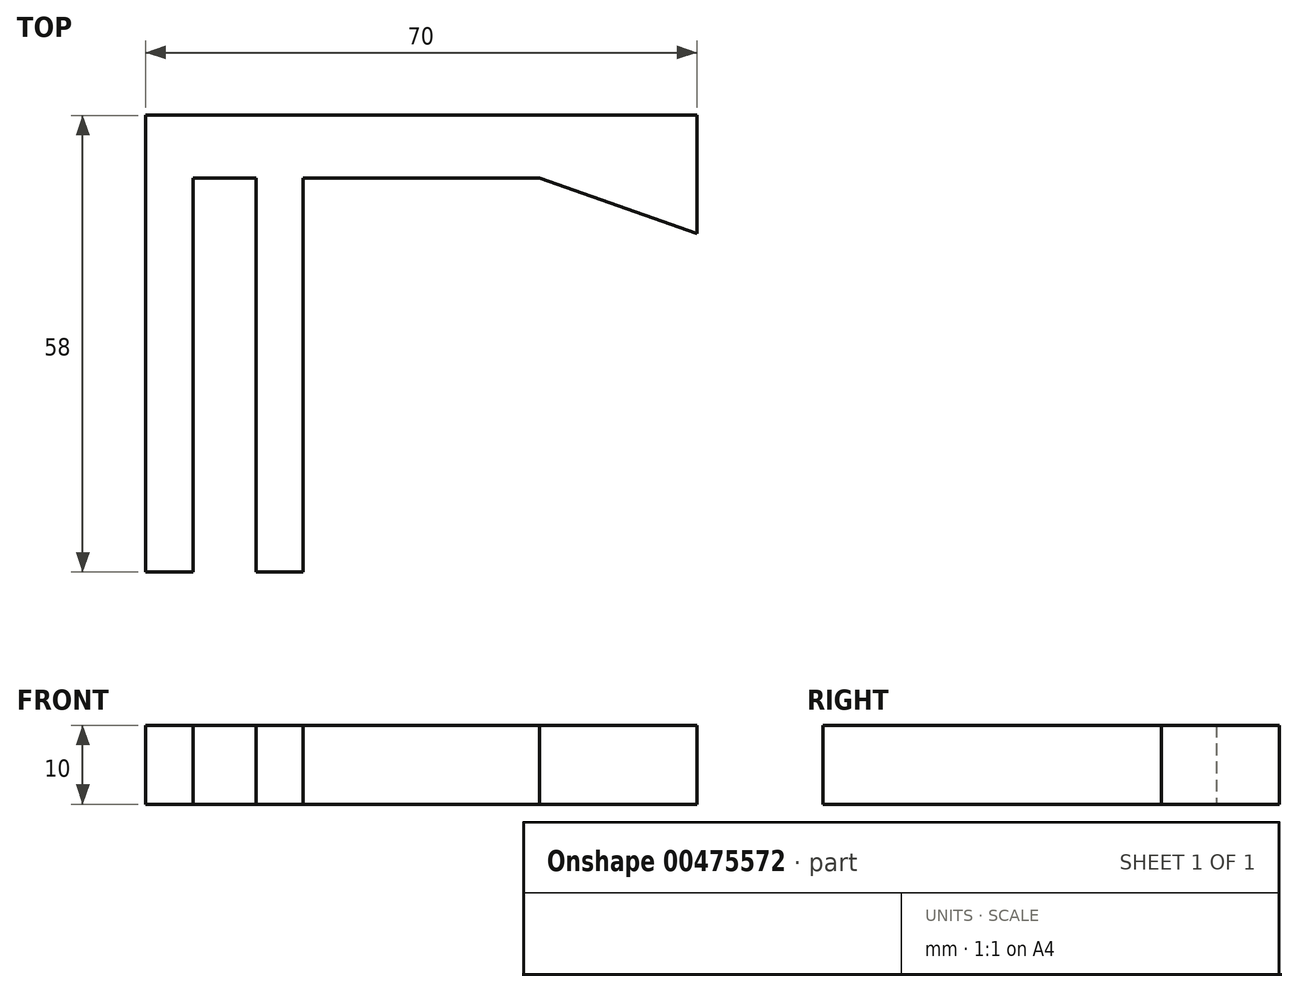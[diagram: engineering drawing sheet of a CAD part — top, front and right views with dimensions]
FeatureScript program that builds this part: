
annotation { "Feature Type Name" : "Feature", "Feature Type Description" : "" }
export const myFeature = defineFeature(function(context is Context, id is Id, definition is map)
    precondition{}
    {
        {
            var Q0;
            Q0=qCreatedBy(makeId("Top.planeOp"),FACE);
            var sketch = newSketch(context, id + "F0", { "sketchPlane" : qUnion([Q0])});
            skLineSegment(sketch, "E0.bottom", {"start": v(-19.46, 25.73) * mm, "end": v(-13.46, 25.73) * mm});
            skLineSegment(sketch, "E0.top", {"start": v(-19.46, -24.27) * mm, "end": v(-13.46, -24.27) * mm});
            skLineSegment(sketch, "E0.left", {"start": v(-19.46, 25.73) * mm, "end": v(-19.46, -24.27) * mm});
            skLineSegment(sketch, "E0.right", {"start": v(-13.46, 25.73) * mm, "end": v(-13.46, -24.27) * mm});
            skLineSegment(sketch, "E1.bottom", {"start": v(-5.46, 25.73) * mm, "end": v(0.54, 25.73) * mm});
            skLineSegment(sketch, "E1.top", {"start": v(-5.46, -24.27) * mm, "end": v(0.54, -24.27) * mm});
            skLineSegment(sketch, "E1.left", {"start": v(-5.46, 25.73) * mm, "end": v(-5.46, -24.27) * mm});
            skLineSegment(sketch, "E1.right", {"start": v(0.54, 25.73) * mm, "end": v(0.54, -24.27) * mm});
            skLineSegment(sketch, "E2.top", {"start": v(-19.46, 33.73) * mm, "end": v(50.54, 33.73) * mm});
            skLineSegment(sketch, "E2.left", {"start": v(-19.46, 25.73) * mm, "end": v(-19.46, 33.73) * mm});
            skLineSegment(sketch, "E3", {"start": v(-19.46, 25.73) * mm, "end": v(30.54, 25.73) * mm});
            skLineSegment(sketch, "E4", {"start": v(50.54, 33.73) * mm, "end": v(50.54, 18.73) * mm});
            skLineSegment(sketch, "E5", {"start": v(50.54, 18.73) * mm, "end": v(30.54, 25.73) * mm});
            skSolve(sketch);
        }
        {
            var Q0;
            Q0=qSketchRegion(id+"F0",true);
            extrude(context, id + "F1", {"entities" : qUnion([Q0]), "depth" : 10 * mm, "offsetDistance" : 25 * mm});
        }
        {
            var Q0;
            Q0=makeQuery(id+"F1.opExtrude","SWEPT_BODY",BODY,{"disambiguationData":[OSD([sQuery(id+"F0.wireOp",EDGE,"E0.top"),sQuery(id+"F0.wireOp",EDGE,"E0.left"),sQuery(id+"F0.wireOp",EDGE,"E0.right"),sQuery(id+"F0.wireOp",EDGE,"E1.top"),sQuery(id+"F0.wireOp",EDGE,"E1.left"),sQuery(id+"F0.wireOp",EDGE,"E1.right"),sQuery(id+"F0.wireOp",EDGE,"E2.top"),sQuery(id+"F0.wireOp",EDGE,"E2.left"),sQuery(id+"F0.wireOp",EDGE,"E3"),sQuery(id+"F0.wireOp",EDGE,"E4"),sQuery(id+"F0.wireOp",EDGE,"E5")])]});
            transform(context, id + "F2", {"entities" : qUnion([Q0]), "transformType" : TransformType.TRANSLATION_3D, "dx" : 0 * mm, "dy" : 0 * mm, "dz" : 0 * mm, "makeCopy" : true});
        }
        {
            var Q0;
            Q0=makeQuery(id+"F2.opPattern","COPY",BODY,{"derivedFrom":makeQuery(id+"F1.opExtrude","SWEPT_BODY",BODY,{"disambiguationData":[OSD([sQuery(id+"F0.wireOp",EDGE,"E0.top"),sQuery(id+"F0.wireOp",EDGE,"E0.left"),sQuery(id+"F0.wireOp",EDGE,"E0.right"),sQuery(id+"F0.wireOp",EDGE,"E1.top"),sQuery(id+"F0.wireOp",EDGE,"E1.left"),sQuery(id+"F0.wireOp",EDGE,"E1.right"),sQuery(id+"F0.wireOp",EDGE,"E2.top"),sQuery(id+"F0.wireOp",EDGE,"E2.left"),sQuery(id+"F0.wireOp",EDGE,"E3"),sQuery(id+"F0.wireOp",EDGE,"E4"),sQuery(id+"F0.wireOp",EDGE,"E5")])]}),"instanceName":"1"});
            deleteBodies(context, id + "F3", {"entities" : qUnion([Q0])});
        }
    });
